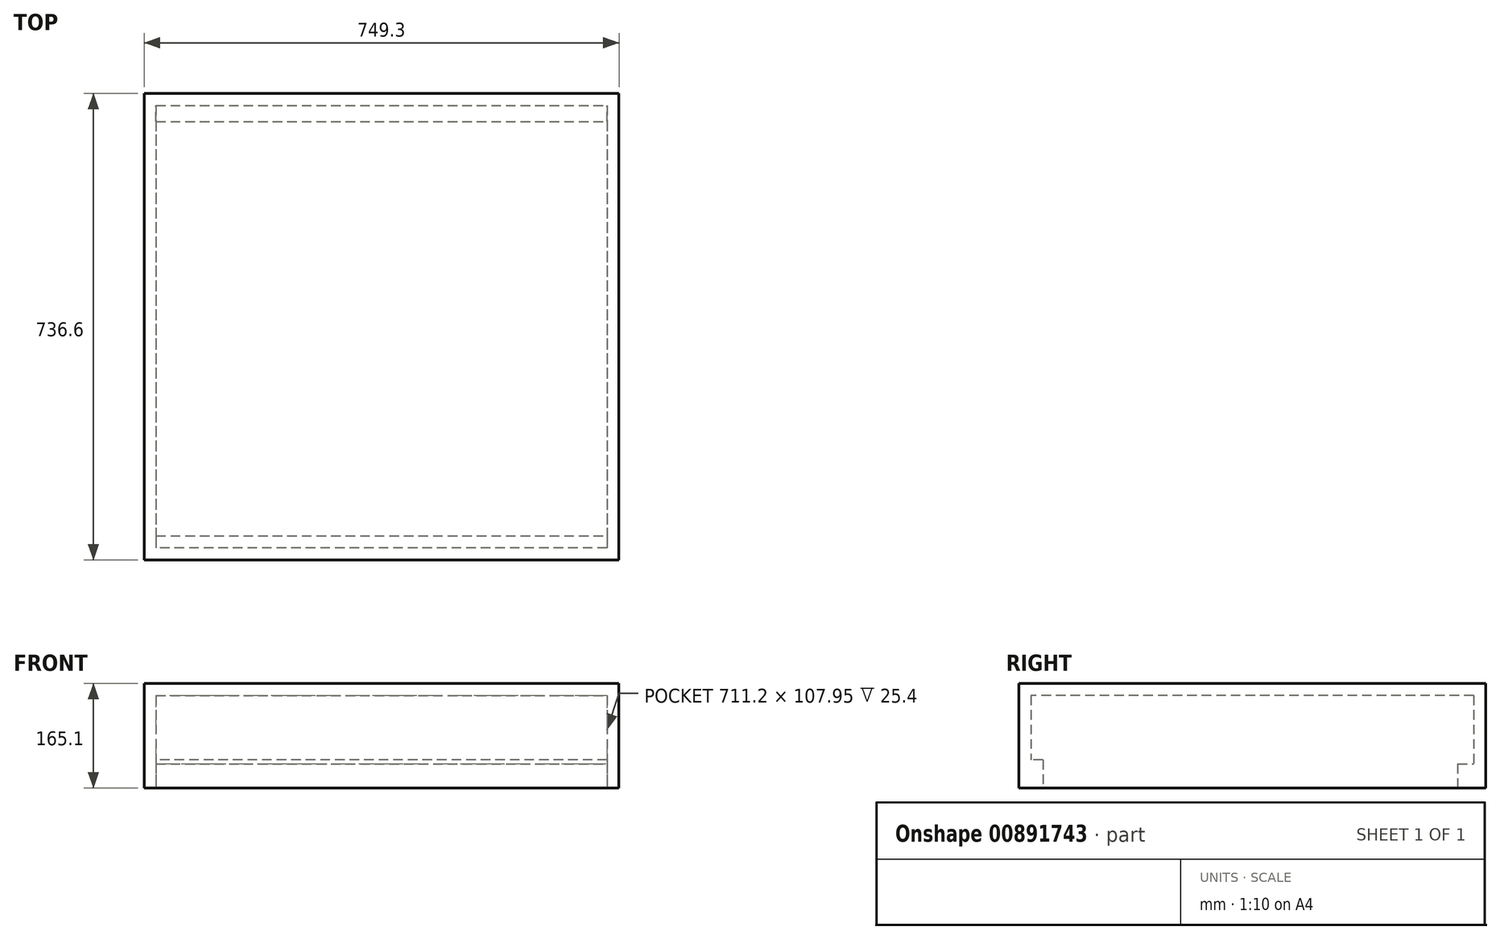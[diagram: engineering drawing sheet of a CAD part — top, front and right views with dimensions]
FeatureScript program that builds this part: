
annotation { "Feature Type Name" : "Feature", "Feature Type Description" : "" }
export const myFeature = defineFeature(function(context is Context, id is Id, definition is map)
    precondition{}
    {
        {
            var Q0;
            Q0=qCreatedBy(makeId("Top.planeOp"),FACE);
            var sketch = newSketch(context, id + "F0", { "sketchPlane" : qUnion([Q0])});
            skLineSegment(sketch, "E0.bottom", {"start": v(-391.82, 540.17) * mm, "end": v(357.48, 540.17) * mm});
            skLineSegment(sketch, "E0.top", {"start": v(-391.82, -196.43) * mm, "end": v(357.48, -196.43) * mm});
            skLineSegment(sketch, "E0.left", {"start": v(-391.82, 540.17) * mm, "end": v(-391.82, -196.43) * mm});
            skLineSegment(sketch, "E0.right", {"start": v(357.48, 540.17) * mm, "end": v(357.48, -196.43) * mm});
            skSolve(sketch);
        }
        {
            var Q0;
            Q0=makeQuery(id+"F0.imprint","IMPRINT",FACE,{"disambiguationData":[TD([[makeQuery(id+"F0.imprint","IMPRINT",EDGE,{"derivedFrom":sQuery(id+"F0.wireOp",EDGE,"E0.bottom")}),-1.0]])]});
            extrude(context, id + "F1", {"entities" : qUnion([Q0]), "depth" : 165.1 * mm});
        }
        {
            var Q0;
            Q0=makeQuery(id+"F1.opExtrude","CAP_FACE",FACE,{"disambiguationData":[OSD([sQuery(id+"F0.wireOp",EDGE,"E0.bottom"),sQuery(id+"F0.wireOp",EDGE,"E0.top"),sQuery(id+"F0.wireOp",EDGE,"E0.left"),sQuery(id+"F0.wireOp",EDGE,"E0.right")])],"isStart":true});
            shell(context, id + "F2", {"entities" : qUnion([Q0]), "thickness" : 19.05 * mm});
        }
        {
            var Q0;
            Q0=makeQuery(id+"F2.opShell","OFFSET_FACE",FACE,{"disambiguationData":[OSD([sQuery(id+"F0.wireOp",EDGE,"E0.bottom")])]});
            var sketch = newSketch(context, id + "F3", { "sketchPlane" : qUnion([Q0])});
            skLineSegment(sketch, "E1.bottom", {"start": v(-372.77, 0) * mm, "end": v(338.43, 0) * mm});
            skLineSegment(sketch, "E1.top", {"start": v(-372.77, 38.1) * mm, "end": v(338.43, 38.1) * mm});
            skLineSegment(sketch, "E1.left", {"start": v(-372.77, 0) * mm, "end": v(-372.77, 38.1) * mm});
            skLineSegment(sketch, "E1.right", {"start": v(338.43, 0) * mm, "end": v(338.43, 38.1) * mm});
            skSolve(sketch);
        }
        {
            var Q0;
            Q0=qSketchRegion(id+"F3",true);
            extrude(context, id + "F4", {"entities" : qUnion([Q0]), "operationType" : NewBodyOperationType.ADD, "depth" : 25.4 * mm});
        }
        {
            var Q0;
            Q0=makeQuery(id+"F2.opShell","OFFSET_FACE",FACE,{"disambiguationData":[OSD([sQuery(id+"F0.wireOp",EDGE,"E0.top")])]});
            var sketch = newSketch(context, id + "F5", { "sketchPlane" : qUnion([Q0])});
            skLineSegment(sketch, "E2.bottom", {"start": v(-338.43, 0) * mm, "end": v(372.77, 0) * mm});
            skLineSegment(sketch, "E2.top", {"start": v(-338.43, 44.45) * mm, "end": v(372.77, 44.45) * mm});
            skLineSegment(sketch, "E2.left", {"start": v(-338.43, 0) * mm, "end": v(-338.43, 44.45) * mm});
            skLineSegment(sketch, "E2.right", {"start": v(372.77, 0) * mm, "end": v(372.77, 44.45) * mm});
            skSolve(sketch);
        }
        {
            var Q0;
            Q0=qSketchRegion(id+"F5",true);
            extrude(context, id + "F6", {"entities" : qUnion([Q0]), "operationType" : NewBodyOperationType.ADD, "depth" : 19.05 * mm});
        }
    });
